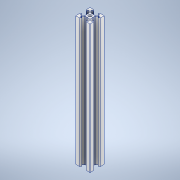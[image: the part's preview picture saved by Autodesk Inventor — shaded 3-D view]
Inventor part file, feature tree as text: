
AUTODESK INVENTOR PART (.ipt)
format: ipt  version: 2021 (Build 250183000, 183)  size: 237,568 bytes
history: native  units: mm
features: sketch x3, extrude x2, fillet x2, other x1, pattern_circular x1, hole x1, projected_geometry x1
ambient origin geometry x8: Origin, YZ Plane, XZ Plane, XY Plane, X Axis, Y Axis, Z Axis, Center Point
bodies: Body1 (feature_tree)
feature tree (11):
  other  "實體1"
  extrude  "擠出1"  Depth=20.0mm
  extrude  "擠出2"  Depth=20.0mm
  fillet  "圓角1"  Radius=180.0mm
  pattern_circular  "環形陣列1"  [2 undecoded]
  hole  "孔1"  [1 undecoded]
  fillet  "圓角2"  Radius=6.2mm
  sketch  "草圖1"
  sketch  "草圖2"
  projected_geometry  "投影迴路1"
  sketch  "草圖3"
note: 3 required parameter values undecoded (feature->parameter linkage not recoverable at this tier; creation-order binding heuristic only, values carry confidence <= 0.55)
